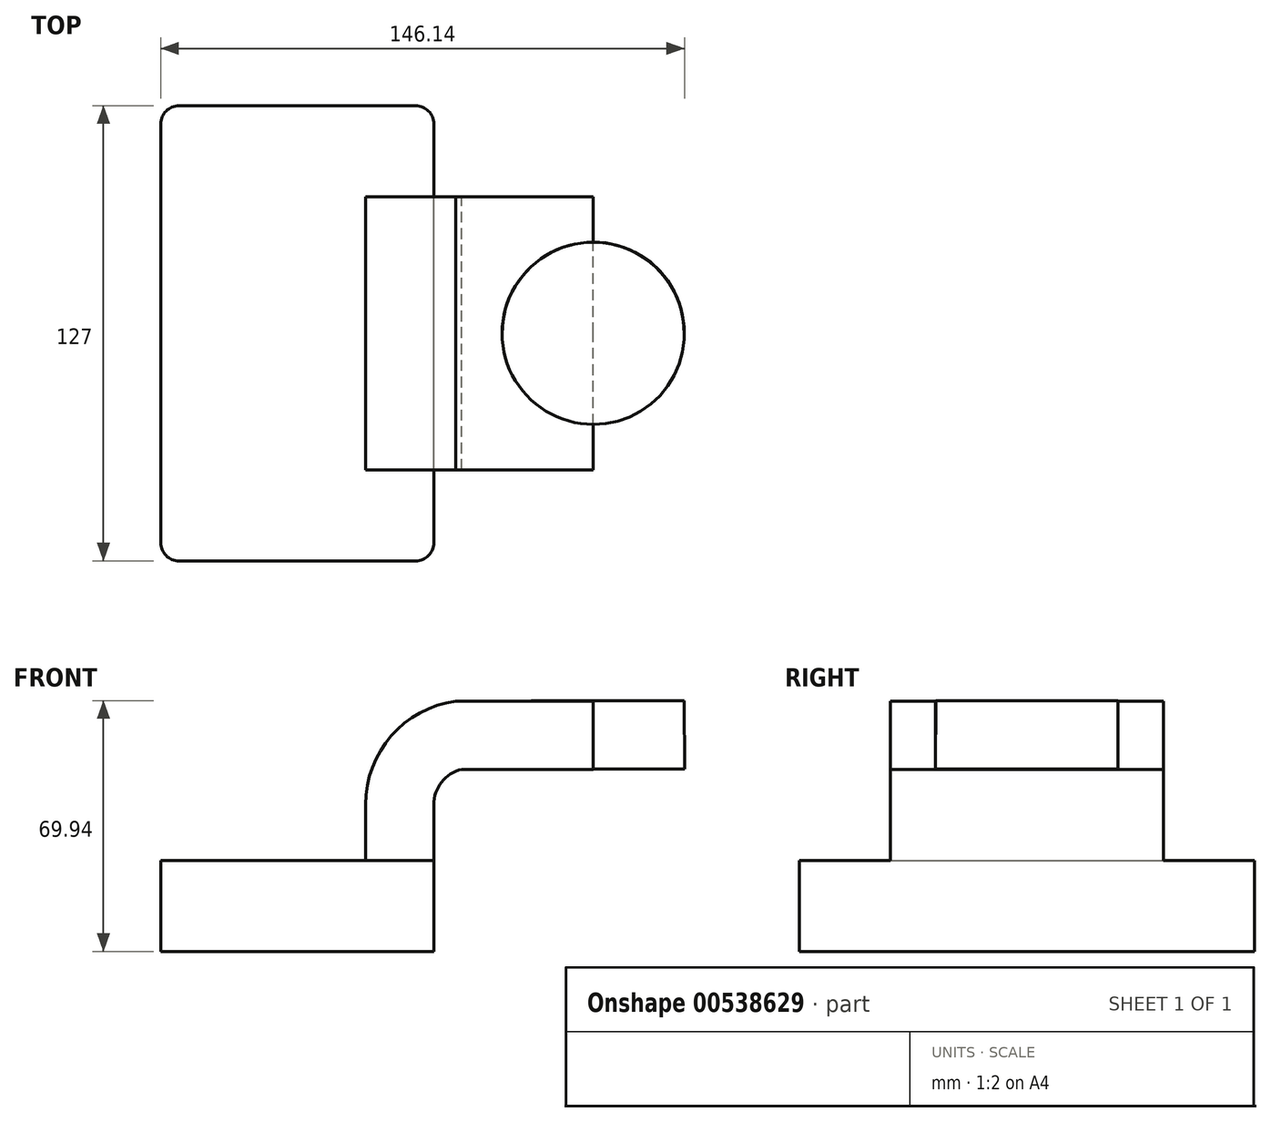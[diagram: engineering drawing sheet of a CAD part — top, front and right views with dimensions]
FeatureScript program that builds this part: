
annotation { "Feature Type Name" : "Feature", "Feature Type Description" : "" }
export const myFeature = defineFeature(function(context is Context, id is Id, definition is map)
    precondition{}
    {
        {
            var Q0;
            Q0=qCreatedBy(makeId("Front.planeOp"),FACE);
            var sketch = newSketch(context, id + "F0", { "sketchPlane" : qUnion([Q0])});
            skLineSegment(sketch, "E0.bottom", {"start": v(38.1, -12.7) * mm, "end": v(-38.1, -12.7) * mm});
            skLineSegment(sketch, "E0.top", {"start": v(38.1, 12.7) * mm, "end": v(-38.1, 12.7) * mm});
            skLineSegment(sketch, "E0.left", {"start": v(38.1, -12.7) * mm, "end": v(38.1, 12.7) * mm});
            skLineSegment(sketch, "E0.right", {"start": v(-38.1, -12.7) * mm, "end": v(-38.1, 12.7) * mm});
            skPoint(sketch, "E0.middle", {"position": v(0, 0) * mm});
            skLineSegment(sketch, "E1.bottom", {"start": v(107.95, 38.1) * mm, "end": v(57.15, 38.1) * mm});
            skLineSegment(sketch, "E1.top", {"start": v(107.95, 63.5) * mm, "end": v(57.15, 63.5) * mm});
            skLineSegment(sketch, "E1.left", {"start": v(107.95, 38.1) * mm, "end": v(107.95, 63.5) * mm});
            skLineSegment(sketch, "E1.right", {"start": v(57.15, 38.1) * mm, "end": v(57.15, 63.5) * mm});
            skPoint(sketch, "E1.middle", {"position": v(82.55, 50.8) * mm});
            skLineSegment(sketch, "E2", {"start": v(38.1, 12.7) * mm, "end": v(38.1, 28.22) * mm});
            skArc(sketch, "E3", {"start": v(38.1, 28.22) * mm, "mid": v(40.28, 34.51) * mm, "end": v(45.9, 38.1) * mm});
            skPoint(sketch, "E3.endSnap0", {"position": v(57.15, 50.8) * mm});
            skLineSegment(sketch, "E4", {"start": v(45.9, 38.1) * mm, "end": v(82.6, 38.1) * mm});
            skLineSegment(sketch, "E5.0", {"start": v(44.23, 57.15) * mm, "end": v(83.1, 57.15) * mm});
            skArc(sketch, "E5.1", {"start": v(19.05, 28.22) * mm, "mid": v(26.23, 47.4) * mm, "end": v(44.23, 57.15) * mm});
            skLineSegment(sketch, "E5.2", {"start": v(19.05, 12.7) * mm, "end": v(19.05, 28.22) * mm});
            skLineSegment(sketch, "E6", {"start": v(82.55, 63.5) * mm, "end": v(82.6, 38.1) * mm});
            skFitSpline(sketch, "E7", {"points": [v(-38.1, 12.7) * mm, v(57.15, 63.5) * mm], "startDerivative": vector(12.71, 128.5) * mm, "endDerivative": vector(171.45, 5.6) * mm});
            skSolve(sketch);
        }
        {
            var Q0;
            Q0=makeQuery(id+"F0.imprint","IMPRINT",FACE,{"disambiguationData":[TD([[makeQuery(id+"F0.imprint","IMPRINT",EDGE,{"derivedFrom":sQuery(id+"F0.wireOp",EDGE,"E0.bottom")}),-1.0]])]});
            extrude(context, id + "F1", {"entities" : qUnion([Q0]), "endBound" : BoundingType.SYMMETRIC, "depth" : 127 * mm, "offsetDistance" : 25.4 * mm});
        }
        {
            var Q0;
            {var subQ1=sQuery(id+"F0.wireOp",EDGE,"E2");Q0=makeQuery(id+"F0.imprint","IMPRINT",FACE,{"disambiguationData":[TD([[makeQuery(id+"F0.imprint","IMPRINT",EDGE,{"derivedFrom":subQ1}),1.0]])]});}
            var Q1;
            {var subQ0=sQuery(id+"F0.wireOp",EDGE,"E4");var subQ1=sQuery(id+"F0.wireOp",EDGE,"E1.right");var subQ2=makeQuery(id+"F0.imprint","INTERSECT",VERTEX,{"derivedFrom":[subQ1,subQ0]});Q1=makeQuery(id+"F0.imprint","IMPRINT",FACE,{"disambiguationData":[TD([[makeQuery(id+"F0.imprint","IMPRINT",EDGE,{"disambiguationData":[TD([[subQ2,-1.0]])],"derivedFrom":subQ1}),-1.0]])]});}
            extrude(context, id + "F2", {"entities" : qUnion([Q0, Q1]), "operationType" : NewBodyOperationType.ADD, "endBound" : BoundingType.SYMMETRIC, "depth" : 76.2 * mm, "offsetDistance" : 25.4 * mm});
        }
        {
            var Q0;
            {var subQ0=sQuery(id+"F0.wireOp",EDGE,"E5.1");Q0=makeQuery(id+"F0.imprint","IMPRINT",FACE,{"disambiguationData":[TD([[makeQuery(id+"F0.imprint","IMPRINT",EDGE,{"derivedFrom":subQ0}),1.0]])]});}
            extrude(context, id + "F3", {"entities" : qUnion([Q0]), "operationType" : NewBodyOperationType.ADD, "endBound" : BoundingType.SYMMETRIC, "depth" : 25.4 * mm, "offsetDistance" : 25.4 * mm});
        }
        {
            var Q0;
            {var subQ5=sQuery(id+"F0.wireOp",EDGE,"E1.bottom");Q0=makeQuery(id+"F0.imprint","IMPRINT",FACE,{"disambiguationData":[TD([[makeQuery(id+"F0.imprint","IMPRINT",EDGE,{"derivedFrom":subQ5}),-1.0]])]});}
            var Q1;
            Q1=sQuery(id+"F0.wireOp",EDGE,"E6");
            revolve(context, id + "F4", {"operationType" : NewBodyOperationType.ADD, "entities" : qUnion([Q0]), "axis" : qUnion([Q1]), "revolveType" : RevolveType.FULL});
        }
        {
            var Q0;
            Q0=makeQuery(id+"F1.opExtrude","CAP_EDGE",EDGE,{"disambiguationData":[OSD([sQuery(id+"F0.wireOp",EDGE,"E0.left")])],"isStart":false});
            var Q1;
            Q1=makeQuery(id+"F1.opExtrude","CAP_EDGE",EDGE,{"disambiguationData":[OSD([sQuery(id+"F0.wireOp",EDGE,"E0.right")])],"isStart":false});
            var Q2;
            Q2=makeQuery(id+"F1.opExtrude","CAP_EDGE",EDGE,{"disambiguationData":[OSD([sQuery(id+"F0.wireOp",EDGE,"E0.left")])],"isStart":true});
            var Q3;
            Q3=makeQuery(id+"F1.opExtrude","CAP_EDGE",EDGE,{"disambiguationData":[OSD([sQuery(id+"F0.wireOp",EDGE,"E0.right")])],"isStart":true});
            fillet(context, id + "F5", {"entities" : qUnion([Q0, Q1, Q2, Q3]), "radius" : 5.08 * mm, "tangentPropagation" : true, "allowEdgeOverflow" : false});
        }
    });
